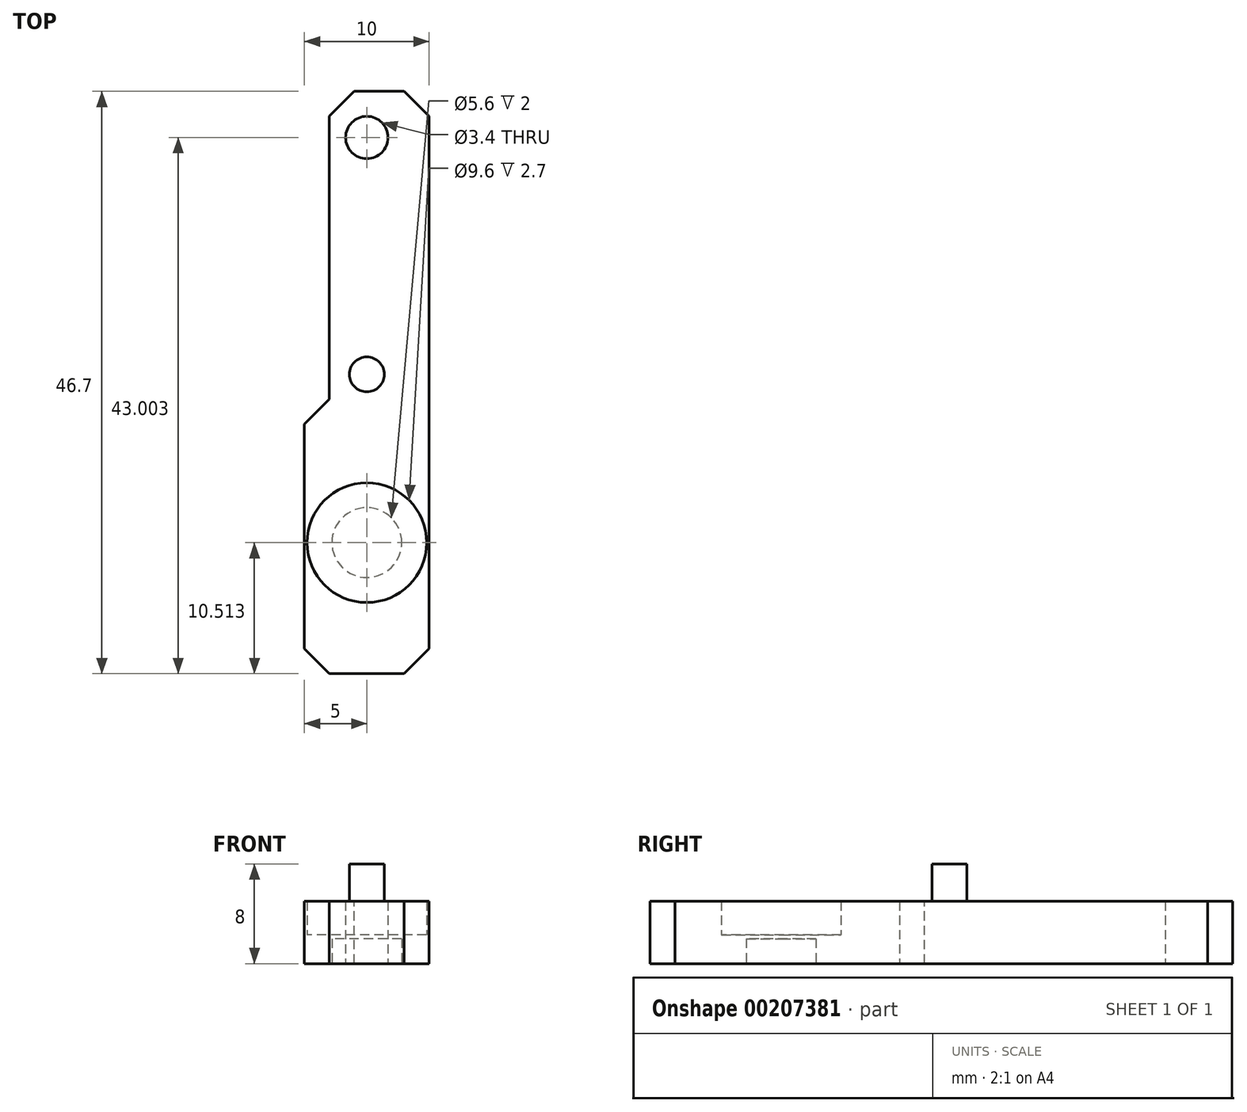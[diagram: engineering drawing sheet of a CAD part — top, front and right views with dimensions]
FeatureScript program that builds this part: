
annotation { "Feature Type Name" : "Feature", "Feature Type Description" : "" }
export const myFeature = defineFeature(function(context is Context, id is Id, definition is map)
    precondition{}
    {
        {
            var Q0;
            Q0=qCreatedBy(makeId("Top.planeOp"),FACE);
            var sketch = newSketch(context, id + "F0", { "sketchPlane" : qUnion([Q0])});
            skLineSegment(sketch, "E0.bottom", {"start": v(-5, -29.26) * mm, "end": v(5, -29.26) * mm});
            skLineSegment(sketch, "E0.right", {"start": v(5, -29.26) * mm, "end": v(5, 17.44) * mm});
            skPoint(sketch, "E1", {"position": v(0, 23.44) * mm});
            skCircle(sketch, "E2", {"center": v(0, -18.75) * mm, "radius": 2.8 * mm});
            skPoint(sketch, "E2.centerSnap0", {"position": v(0, -29.26) * mm});
            skCircle(sketch, "E3", {"center": v(0, -5.26) * mm, "radius": 1.4 * mm});
            skCircle(sketch, "E4", {"center": v(0, 13.74) * mm, "radius": 1.7 * mm});
            skLineSegment(sketch, "E5", {"start": v(-5, -9.26) * mm, "end": v(5, -9.26) * mm});
            skCircle(sketch, "E6", {"center": v(0, -18.75) * mm, "radius": 4.8 * mm});
            skLineSegment(sketch, "E7", {"start": v(5, 17.44) * mm, "end": v(-3, 17.44) * mm});
            skLineSegment(sketch, "E8", {"start": v(-3, 17.44) * mm, "end": v(-3, -9.26) * mm});
            skLineSegment(sketch, "E9", {"start": v(-5, -9.26) * mm, "end": v(-5, -29.26) * mm});
            skSolve(sketch);
        }
        {
            var Q0;
            Q0=makeQuery(id+"F0.imprint","IMPRINT",FACE,{"disambiguationData":[TD([[makeQuery(id+"F0.imprint","IMPRINT",EDGE,{"derivedFrom":sQuery(id+"F0.wireOp",EDGE,"E3")}),-1.0]])]});
            var Q1;
            {var subQ5=sQuery(id+"F0.wireOp",EDGE,"E0.bottom");Q1=makeQuery(id+"F0.imprint","IMPRINT",FACE,{"disambiguationData":[TD([[makeQuery(id+"F0.imprint","IMPRINT",EDGE,{"derivedFrom":subQ5}),1.0]])]});}
            extrude(context, id + "F1", {"entities" : qUnion([Q0, Q1]), "depth" : 5 * mm});
        }
        {
            var Q0;
            Q0=makeQuery(id+"F0.imprint","IMPRINT",FACE,{"disambiguationData":[TD([[makeQuery(id+"F0.imprint","IMPRINT",EDGE,{"derivedFrom":sQuery(id+"F0.wireOp",EDGE,"E3")}),1.0]])]});
            extrude(context, id + "F2", {"entities" : qUnion([Q0]), "operationType" : NewBodyOperationType.ADD, "depth" : 8 * mm});
        }
        {
            var Q0;
            Q0=makeQuery(id+"F0.imprint","IMPRINT",FACE,{"disambiguationData":[TD([[makeQuery(id+"F0.imprint","IMPRINT",EDGE,{"derivedFrom":sQuery(id+"F0.wireOp",EDGE,"E2")}),-1.0]])]});
            extrude(context, id + "F3", {"entities" : qUnion([Q0]), "operationType" : NewBodyOperationType.ADD, "depth" : 2.3 * mm});
        }
        {
            var Q0;
            Q0=makeQuery(id+"F0.imprint","IMPRINT",FACE,{"disambiguationData":[TD([[makeQuery(id+"F0.imprint","IMPRINT",EDGE,{"derivedFrom":sQuery(id+"F0.wireOp",EDGE,"E2")}),1.0]])]});
            extrude(context, id + "F4", {"entities" : qUnion([Q0]), "operationType" : NewBodyOperationType.ADD, "depth" : 2.3 * mm, "hasSecondDirection" : true, "secondDirectionOppositeDirection" : false, "secondDirectionDepth" : 2 * mm});
        }
        {
            var Q0;
            Q0=makeQuery(id+"F1.opExtrude","SWEPT_EDGE",EDGE,{"disambiguationData":[OSD([sQuery(id+"F0.wireOp",EDGE,"E5"),sQuery(id+"F0.wireOp",EDGE,"E8")])]});
            var Q1;
            Q1=makeQuery(id+"F1.opExtrude","SWEPT_EDGE",EDGE,{"disambiguationData":[OSD([sQuery(id+"F0.wireOp",EDGE,"E7"),sQuery(id+"F0.wireOp",EDGE,"E8")])]});
            var Q2;
            Q2=makeQuery(id+"F1.opExtrude","SWEPT_EDGE",EDGE,{"disambiguationData":[OSD([sQuery(id+"F0.wireOp",EDGE,"E0.right"),sQuery(id+"F0.wireOp",EDGE,"E7")])]});
            var Q3;
            Q3=makeQuery(id+"F1.opExtrude","SWEPT_EDGE",EDGE,{"disambiguationData":[OSD([sQuery(id+"F0.wireOp",EDGE,"E0.bottom"),sQuery(id+"F0.wireOp",EDGE,"E0.right")])]});
            var Q4;
            Q4=makeQuery(id+"F1.opExtrude","SWEPT_EDGE",EDGE,{"disambiguationData":[OSD([sQuery(id+"F0.wireOp",EDGE,"E0.bottom"),sQuery(id+"F0.wireOp",EDGE,"E9")])]});
            chamfer(context, id + "F5", {"entities" : qUnion([Q0, Q1, Q2, Q3, Q4]), "width" : 2 * mm, "tangentPropagation" : true});
        }
    });
